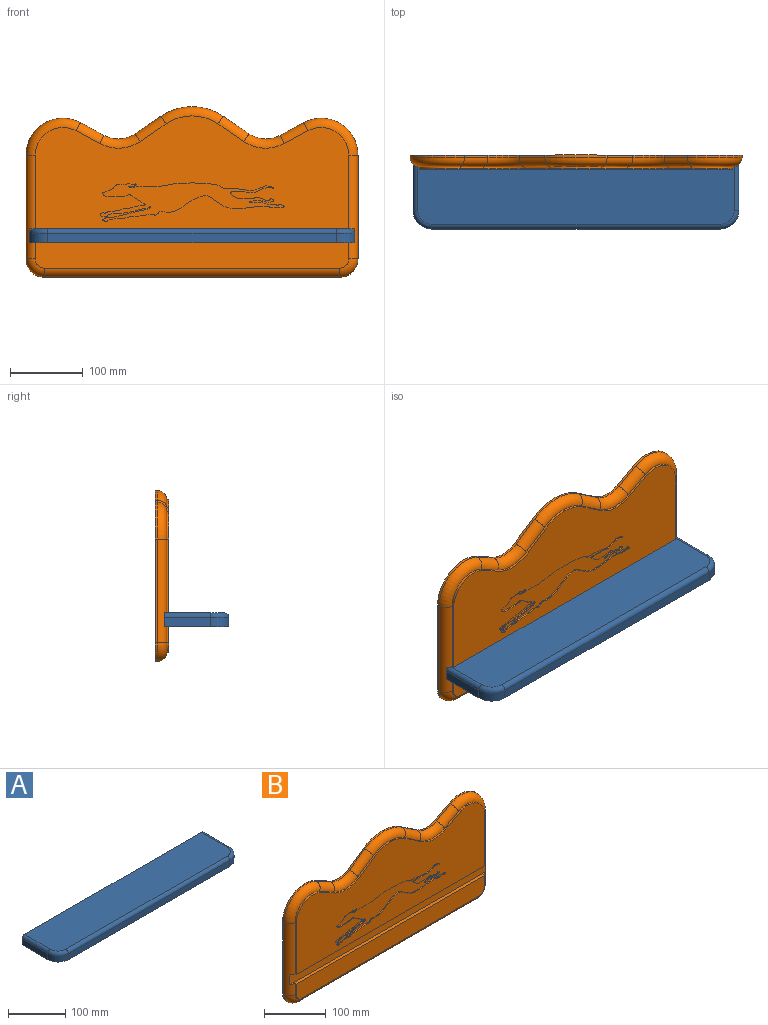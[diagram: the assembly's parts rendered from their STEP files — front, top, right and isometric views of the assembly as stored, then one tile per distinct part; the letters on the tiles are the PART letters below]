
ASSEMBLY  parts=2 mates=1
PART A: 13 faces, bbox 452.8x91x19.1 mm
  f0: plane 448.6x88.9mm, normal (0,0,-1), area 39603.7mm2, adj f2,f3,f4,f5,f6,f7
  f1: plane 435.9x82.55mm, normal (0,0,1), area 35827.8mm2, adj f5,f8,f9,f10,f11,f12
  f2: plane 63.5x12.7mm, normal (-1,0,0), area 806.4mm2, adj f0,f5,f7,f8
  f3: plane 397.8x12.7mm, normal (0,-1,0), area 5052.1mm2, adj f0,f6,f7,f10
  f4: plane 63.5x12.7mm, normal (1,0,0), area 806.4mm2, adj f0,f5,f6,f12
  f5: plane 448.6x19.05mm, normal (0,1,0), area 8528.5mm2, adj f0,f1,f2,f4,f8,f12
  f6: cylinder r=25.4mm len=25.4mm, axis (0,0,1), area 506.7mm2, adj f0,f3,f4,f11
  f7: cylinder r=25.4mm len=25.4mm, axis (0,0,1), area 506.7mm2, adj f0,f2,f3,f9
  f8: cylinder r=6.35mm len=63.5mm, axis (0,1,0), area 633.4mm2, adj f1,f2,f5,f9
  f9: torus R=19.05mm, axis (0,0,1), area 361.8mm2, adj f1,f7,f8,f10
  f10: cylinder r=6.35mm len=397.8mm, axis (1,0,0), area 3967.9mm2, adj f1,f3,f9,f11
  f11: torus R=19.05mm, axis (0,0,1), area 361.8mm2, adj f1,f6,f10,f12
  f12: cylinder r=6.35mm len=63.5mm, axis (0,1,0), area 633.4mm2, adj f1,f4,f5,f11
PART B: 58 faces, bbox 465.6x24.9x243.3 mm
  f0: plane 431.8x155.58mm, normal (0,-1,0), area 50606.1mm2, adj f1,f2,f20,f21,f22,f23,f24,f25
  f1: plane 101.6x3.18mm, normal (1,0,0), area 322.6mm2, adj f0,f4,f27,f47
  f2: plane 101.6x3.18mm, normal (-1,0,0), area 322.6mm2, adj f0,f3,f33,f47
  f3: cylinder r=12.7mm len=142.88mm, axis (0,0,1), area 2675.4mm2, adj f2,f6,f32,f35,f36,f47,f48,f49
  f4: cylinder r=12.7mm len=142.88mm, axis (0,0,-1), area 2675.4mm2, adj f1,f8,f28,f39,f42,f47,f48,f49
  f5: plane 32.46x17.52mm, normal (0.48,0,0.88), area 117.1mm2, adj f12,f13,f19,f38
  f6: plane 142.88x3.18mm, normal (-1,0,0), area 453.6mm2, adj f3,f13,f14,f19
  f7: plane 406.4x3.18mm, normal (0,0,-1), area 1290.3mm2, adj f14,f15,f19,f37
  f8: plane 142.88x3.18mm, normal (1,0,0), area 453.6mm2, adj f4,f15,f16,f19
  f9: plane 32.46x17.52mm, normal (-0.48,0,0.88), area 117.1mm2, adj f16,f17,f19,f44
  f10: plane 35.64x24.18mm, normal (0.56,0,0.83), area 136.7mm2, adj f17,f18,f19,f45
  f11: plane 35.64x24.18mm, normal (-0.56,0,0.83), area 136.7mm2, adj f12,f18,f19,f41
  f12: cylinder r=41.27mm len=42.78mm, axis (0,1,0), area 143mm2, adj f5,f11,f19,f40
  f13: cylinder r=50.8mm len=74.93mm, axis (0,1,0), area 333.2mm2, adj f5,f6,f19,f36
  f14: cylinder r=25.4mm len=25.4mm, axis (0,1,0), area 126.7mm2, adj f6,f7,f19,f35
  f15: cylinder r=25.4mm len=25.4mm, axis (0,1,0), area 126.7mm2, adj f7,f8,f19,f39
  f16: cylinder r=50.8mm len=74.93mm, axis (0,1,0), area 333.2mm2, adj f8,f9,f19,f42
  f17: cylinder r=41.27mm len=42.78mm, axis (0,1,0), area 143mm2, adj f9,f10,f19,f46
  f18: cylinder r=76.2mm len=85.57mm, axis (0,1,0), area 288.5mm2, adj f10,f11,f19,f43
  f19: plane 457.2x234.95mm, normal (0,1,0), area 95770.4mm2, adj f5,f6,f7,f8,f9,f10,f11,f12
  f20: plane 32.46x17.52mm, normal (0.48,0,0.88), area 117.1mm2, adj f0,f21,f33,f38
  f21: cylinder r=53.98mm len=55.95mm, axis (0,-1,0), area 187mm2, adj f0,f20,f22,f40
  f22: plane 35.64x24.18mm, normal (-0.56,0,0.83), area 136.7mm2, adj f0,f21,f23,f41
  f23: cylinder r=63.5mm len=71.31mm, axis (0,-1,0), area 240.4mm2, adj f0,f22,f24,f43
  f24: plane 35.64x24.18mm, normal (0.56,0,0.83), area 136.7mm2, adj f0,f23,f25,f45
  f25: cylinder r=53.98mm len=55.95mm, axis (0,-1,0), area 187mm2, adj f0,f24,f26,f46
  f26: plane 32.46x17.52mm, normal (-0.48,0,0.88), area 117.1mm2, adj f0,f25,f27,f44
  f27: cylinder r=38.1mm len=56.2mm, axis (0,-1,0), area 249.9mm2, adj f0,f1,f26,f42
  f28: plane 22.23x3.18mm, normal (1,0,0), area 70.6mm2, adj f4,f29,f34,f48
  f29: cylinder r=12.7mm len=12.7mm, axis (0,-1,0), area 63.3mm2, adj f28,f30,f34,f39
  f30: plane 406.4x3.18mm, normal (0,0,-1), area 1290.3mm2, adj f29,f31,f34,f37
  f31: cylinder r=12.7mm len=12.7mm, axis (0,-1,0), area 63.3mm2, adj f30,f32,f34,f35
  f32: plane 22.23x3.18mm, normal (-1,0,0), area 70.6mm2, adj f3,f31,f34,f48
  f33: cylinder r=38.1mm len=56.2mm, axis (0,-1,0), area 249.9mm2, adj f0,f2,f20,f36
  f34: plane 431.8x34.93mm, normal (0,-1,0), area 15011.4mm2, adj f28,f29,f30,f31,f32,f48
  f35: torus R=12.7mm, axis (0,-1,0), area 651.3mm2, adj f3,f14,f31,f37
  f36: torus R=38.1mm, axis (0,-1,0), area 1903.3mm2, adj f3,f13,f33,f38
  f37: cylinder r=12.7mm len=406.4mm, axis (-1,0,0), area 8107.3mm2, adj f7,f30,f35,f39
  f38: cylinder r=12.7mm len=38.5mm, axis (0.88,0,-0.48), area 735.9mm2, adj f5,f20,f36,f40
  f39: torus R=12.7mm, axis (0,-1,0), area 651.3mm2, adj f4,f15,f29,f37
  f40: torus R=53.98mm, axis (0,-1,0), area 998.9mm2, adj f12,f21,f38,f41
  f41: cylinder r=12.7mm len=42.77mm, axis (0.83,0,0.56), area 859.2mm2, adj f11,f22,f40,f43
  f42: torus R=38.1mm, axis (0,-1,0), area 1903.3mm2, adj f4,f16,f27,f44
  f43: torus R=63.5mm, axis (0,-1,0), area 1702.8mm2, adj f18,f23,f41,f45
  f44: cylinder r=12.7mm len=38.5mm, axis (0.88,0,0.48), area 735.9mm2, adj f9,f26,f42,f46
  f45: cylinder r=12.7mm len=42.77mm, axis (0.83,0,-0.56), area 859.2mm2, adj f10,f24,f43,f46
  f46: torus R=53.98mm, axis (0,-1,0), area 998.9mm2, adj f17,f25,f44,f45
  f47: plane 448.6x6.35mm, normal (0,0,-1), area 2778.5mm2, adj f0,f1,f2,f3,f4,f49
  f48: plane 448.6x6.35mm, normal (0,0,1), area 2778.5mm2, adj f3,f4,f28,f32,f34,f49
  f49: plane 448.6x19.05mm, normal (0,-1,0), area 8545.8mm2, adj f3,f4,f47,f48
  f50: extruded ~56.23x14.02mm, area 100.1mm2, adj f0,f51,f56,f57
  f51: extruded ~67.38x18.82mm, area 321.9mm2, adj f0,f50,f52,f57
  f52: extruded ~17.07x6.24mm, area 55.2mm2, adj f0,f51,f53,f57
  f53: extruded ~53.03x5.86mm, area 84.7mm2, adj f0,f52,f54,f57
  f54: extruded ~177.58x26.02mm, area 564.6mm2, adj f0,f53,f55,f57
  f55: extruded ~172.19x21.64mm, area 405.8mm2, adj f0,f54,f56,f57
  f56: extruded ~64x13.3mm, area 145.1mm2, adj f0,f50,f55,f57
  f57: plane 253.69x53.42mm, normal (0,-1,0), area 5629.8mm2, adj f50,f51,f52,f53,f54,f55,f56
PLACE A t=(14.99,-45.17,9.63)mm
PLACE B t=(14.99,-45.17,9.61)mm
MATE fastened A.f5 <-> B.f49  axis (0,1,0) through (14.99,-57.87,-50.71)mm
